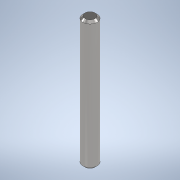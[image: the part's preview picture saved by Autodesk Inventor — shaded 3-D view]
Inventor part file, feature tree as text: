
AUTODESK INVENTOR PART (.ipt)
format: ipt  version: 2020 (Build 240168000, 168)  size: 103,424 bytes
history: native  units: in
note: dims shown in document units (in); Inventor stores cm internally (conversion verified against a paired STEP export)
features: extrude x1, chamfer x1, sketch x1
ambient origin geometry x8: Origin, YZ Plane, XZ Plane, XY Plane, X Axis, Y Axis, Z Axis, Center Point
bodies: Solid1 (feature_tree)
feature tree (3):
  extrude  "Extrusion1"  Depth=4.5in TaperAngle=0.0deg
  chamfer  "Chamfer1"  Distance=0.075in Angle=45.0deg
  sketch  "Sketch1"  dims[d0=0.5in d1=4.5in d2=0.0in d3=0.075in d4=0.125in d5=45.0deg]
